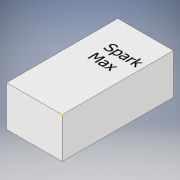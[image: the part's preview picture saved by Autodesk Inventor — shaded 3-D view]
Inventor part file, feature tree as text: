
AUTODESK INVENTOR PART (.ipt)
format: ipt  version: 2019 (Build 230136000, 136)  size: 99,328 bytes
history: native  units: in
note: dims shown in document units (in); Inventor stores cm internally (conversion verified against a paired STEP export)
features: sketch x2, extrude x1
ambient origin geometry x8: Origin, YZ Plane, XZ Plane, XY Plane, X Axis, Y Axis, Z Axis, Center Point
bodies: Solid1 (feature_tree)
feature tree (3):
  extrude  "Extrusion1"  Depth=1.378in
  sketch  "Sketch2"  dims[d2=1.0039in d3=0.0in]
  sketch  "Sketch1"  dims[d0=2.7559in d1=1.378in]
